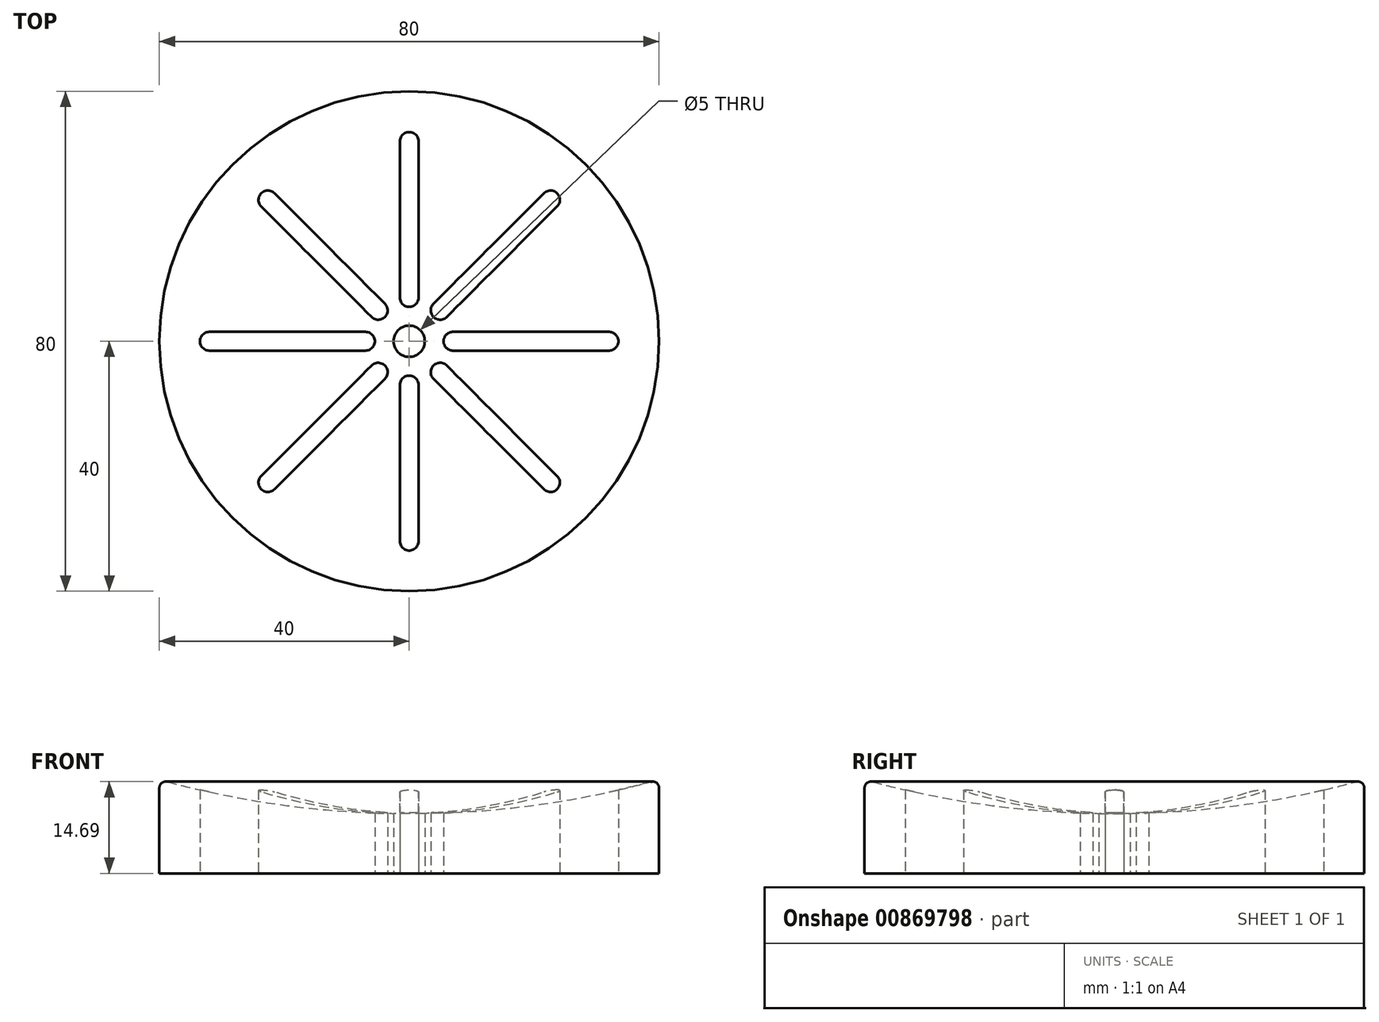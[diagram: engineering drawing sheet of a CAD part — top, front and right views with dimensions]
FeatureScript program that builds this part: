
annotation { "Feature Type Name" : "Feature", "Feature Type Description" : "" }
export const myFeature = defineFeature(function(context is Context, id is Id, definition is map)
    precondition{}
    {
        {
            var Q0;
            Q0=qCreatedBy(makeId("Top.planeOp"),FACE);
            var sketch = newSketch(context, id + "F0", { "sketchPlane" : qUnion([Q0])});
            skCircle(sketch, "E0", {"center": v(0, 0) * mm, "radius": 40 * mm});
            skSolve(sketch);
        }
        {
            var Q0;
            Q0 = qSketchRegion(id + "F0", true);
            extrude(context, id + "F1", {"entities" : qUnion([Q0]), "depth" : 15 * mm, "offsetDistance" : 25 * mm});
        }
        {
            var Q0;
            Q0=qCreatedBy(makeId("Front.planeOp"),FACE);
            var sketch = newSketch(context, id + "F2", { "sketchPlane" : qUnion([Q0])});
            skLineSegment(sketch, "E1.0.0", {"start": v(0, 15) * mm, "end": v(40, 15) * mm});
            skLineSegment(sketch, "E2", {"start": v(0, 15) * mm, "end": v(0, 9.57) * mm});
            skArc(sketch, "E3.trimOffspring", {"start": v(0, 9.57) * mm, "mid": v(20.18, 10.93) * mm, "end": v(40, 15) * mm});
            skSolve(sketch);
        }
        {
            var Q0;
            Q0 = qSketchRegion(id + "F2", true);
            var Q1;
            Q1=sQuery(id+"F2.wireOp",EDGE,"E2");
            revolve(context, id + "F3", {"operationType" : NewBodyOperationType.REMOVE, "surfaceOperationType" : NewSurfaceOperationType.NEW, "entities" : qUnion([Q0]), "axis" : qUnion([Q1]), "revolveType" : RevolveType.FULL, "oppositeDirection" : true});
        }
        {
            var Q0;
            Q0=makeQuery(id+"F3.boolean.opBoolean","COPY",FACE,{"derivedFrom":makeQuery(id+"F3.opRevolve","SWEPT_FACE",FACE,{"disambiguationData":[OSD([sQuery(id+"F2.wireOp",EDGE,"E3.trimOffspring")])]})});
            fillet(context, id + "F4", {"entities" : qUnion([Q0]), "radius" : 1 * mm, "tangentPropagation" : true, "allowEdgeOverflow" : false});
        }
        {
            var Q0;
            Q0=qCreatedBy(makeId("Top.planeOp"),FACE);
            var sketch = newSketch(context, id + "F5", { "sketchPlane" : qUnion([Q0])});
            skCircle(sketch, "E4", {"center": v(0, 0) * mm, "radius": 2.5 * mm});
            skArc(sketch, "E5", {"start": v(-1.5, 7) * mm, "mid": v(0, 5.5) * mm, "end": v(1.5, 7) * mm});
            skArc(sketch, "E6", {"start": v(1.5, 32) * mm, "mid": v(0, 33.5) * mm, "end": v(-1.5, 32) * mm});
            skLineSegment(sketch, "E7", {"start": v(-1.5, 32) * mm, "end": v(-1.5, 7) * mm});
            skLineSegment(sketch, "E8", {"start": v(1.5, 32) * mm, "end": v(1.5, 7) * mm});
            skArc(sketch, "E9.1.0", {"start": v(-21.57, 23.69) * mm, "mid": v(-23.69, 23.69) * mm, "end": v(-23.69, 21.57) * mm});
            skLineSegment(sketch, "E9.1.1", {"start": v(-23.69, 21.57) * mm, "end": v(-6.01, 3.89) * mm});
            skLineSegment(sketch, "E9.1.2", {"start": v(-21.57, 23.69) * mm, "end": v(-3.89, 6.01) * mm});
            skArc(sketch, "E9.1.3", {"start": v(-6.01, 3.89) * mm, "mid": v(-3.89, 3.89) * mm, "end": v(-3.89, 6.01) * mm});
            skArc(sketch, "E9.2.0", {"start": v(-32, 1.5) * mm, "mid": v(-33.5, 0) * mm, "end": v(-32, -1.5) * mm});
            skLineSegment(sketch, "E9.2.1", {"start": v(-32, -1.5) * mm, "end": v(-7, -1.5) * mm});
            skLineSegment(sketch, "E9.2.2", {"start": v(-32, 1.5) * mm, "end": v(-7, 1.5) * mm});
            skArc(sketch, "E9.2.3", {"start": v(-7, -1.5) * mm, "mid": v(-5.5, 0) * mm, "end": v(-7, 1.5) * mm});
            skArc(sketch, "E9.3.0", {"start": v(-23.69, -21.57) * mm, "mid": v(-23.69, -23.69) * mm, "end": v(-21.57, -23.69) * mm});
            skLineSegment(sketch, "E9.3.1", {"start": v(-21.57, -23.69) * mm, "end": v(-3.89, -6.01) * mm});
            skLineSegment(sketch, "E9.3.2", {"start": v(-23.69, -21.57) * mm, "end": v(-6.01, -3.89) * mm});
            skArc(sketch, "E9.3.3", {"start": v(-3.89, -6.01) * mm, "mid": v(-3.89, -3.89) * mm, "end": v(-6.01, -3.89) * mm});
            skArc(sketch, "E9.4.0", {"start": v(-1.5, -32) * mm, "mid": v(0, -33.5) * mm, "end": v(1.5, -32) * mm});
            skLineSegment(sketch, "E9.4.1", {"start": v(1.5, -32) * mm, "end": v(1.5, -7) * mm});
            skLineSegment(sketch, "E9.4.2", {"start": v(-1.5, -32) * mm, "end": v(-1.5, -7) * mm});
            skArc(sketch, "E9.4.3", {"start": v(1.5, -7) * mm, "mid": v(0, -5.5) * mm, "end": v(-1.5, -7) * mm});
            skArc(sketch, "E9.5.0", {"start": v(21.57, -23.69) * mm, "mid": v(23.69, -23.69) * mm, "end": v(23.69, -21.57) * mm});
            skLineSegment(sketch, "E9.5.1", {"start": v(23.69, -21.57) * mm, "end": v(6.01, -3.89) * mm});
            skLineSegment(sketch, "E9.5.2", {"start": v(21.57, -23.69) * mm, "end": v(3.89, -6.01) * mm});
            skArc(sketch, "E9.5.3", {"start": v(6.01, -3.89) * mm, "mid": v(3.89, -3.89) * mm, "end": v(3.89, -6.01) * mm});
            skArc(sketch, "E9.6.0", {"start": v(32, -1.5) * mm, "mid": v(33.5, 0) * mm, "end": v(32, 1.5) * mm});
            skLineSegment(sketch, "E9.6.1", {"start": v(32, 1.5) * mm, "end": v(7, 1.5) * mm});
            skLineSegment(sketch, "E9.6.2", {"start": v(32, -1.5) * mm, "end": v(7, -1.5) * mm});
            skArc(sketch, "E9.6.3", {"start": v(7, 1.5) * mm, "mid": v(5.5, 0) * mm, "end": v(7, -1.5) * mm});
            skArc(sketch, "E9.7.0", {"start": v(23.69, 21.57) * mm, "mid": v(23.69, 23.69) * mm, "end": v(21.57, 23.69) * mm});
            skLineSegment(sketch, "E9.7.1", {"start": v(21.57, 23.69) * mm, "end": v(3.89, 6.01) * mm});
            skLineSegment(sketch, "E9.7.2", {"start": v(23.69, 21.57) * mm, "end": v(6.01, 3.89) * mm});
            skArc(sketch, "E9.7.3", {"start": v(3.89, 6.01) * mm, "mid": v(3.89, 3.89) * mm, "end": v(6.01, 3.89) * mm});
            skSolve(sketch);
        }
        {
            var Q0;
            Q0 = qSketchRegion(id + "F5", true);
            extrude(context, id + "F6", {"entities" : qUnion([Q0]), "operationType" : NewBodyOperationType.REMOVE, "depth" : 25 * mm, "offsetDistance" : 25 * mm});
        }
    });
